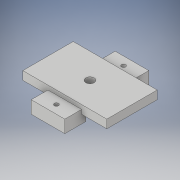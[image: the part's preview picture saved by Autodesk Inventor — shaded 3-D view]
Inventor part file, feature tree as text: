
AUTODESK INVENTOR PART (.ipt)
format: ipt  version: 2017 (Build 210142000, 142)  size: 137,216 bytes
history: native  units: in
note: dims shown in document units (in); Inventor stores cm internally (conversion verified against a paired STEP export)
features: extrude x3, sketch x3, projected_geometry x2
ambient origin geometry x8: Origin, YZ Plane, XZ Plane, XY Plane, X Axis, Y Axis, Z Axis, Center Point
bodies: Solid1 (feature_tree)
feature tree (8):
  extrude  "Extrusion1"  Depth=1.5in
  extrude  "Extrusion2"  Depth=1.25in
  extrude  "Extrusion3"  Depth=0.25in
  sketch  "Sketch1"  dims[d0=2.5in d1=1.5in]
  sketch  "Sketch2"  dims[d2=0.25in d3=0.0in d4=1.25in]
  projected_geometry  "Projected Loop1"
  sketch  "Sketch3"  dims[d5=90.0deg d6=0.25in d7=0.25in d8=0.0in d9=0.5in d10=1.25in d11=2.5in d12=1.0in d13=0.625in d14=1.0in d15=90.0deg d16=0.125in d17=0.25in d18=0.125in d19=0.0in d20=0.0in]
  projected_geometry  "Projected Loop2"
